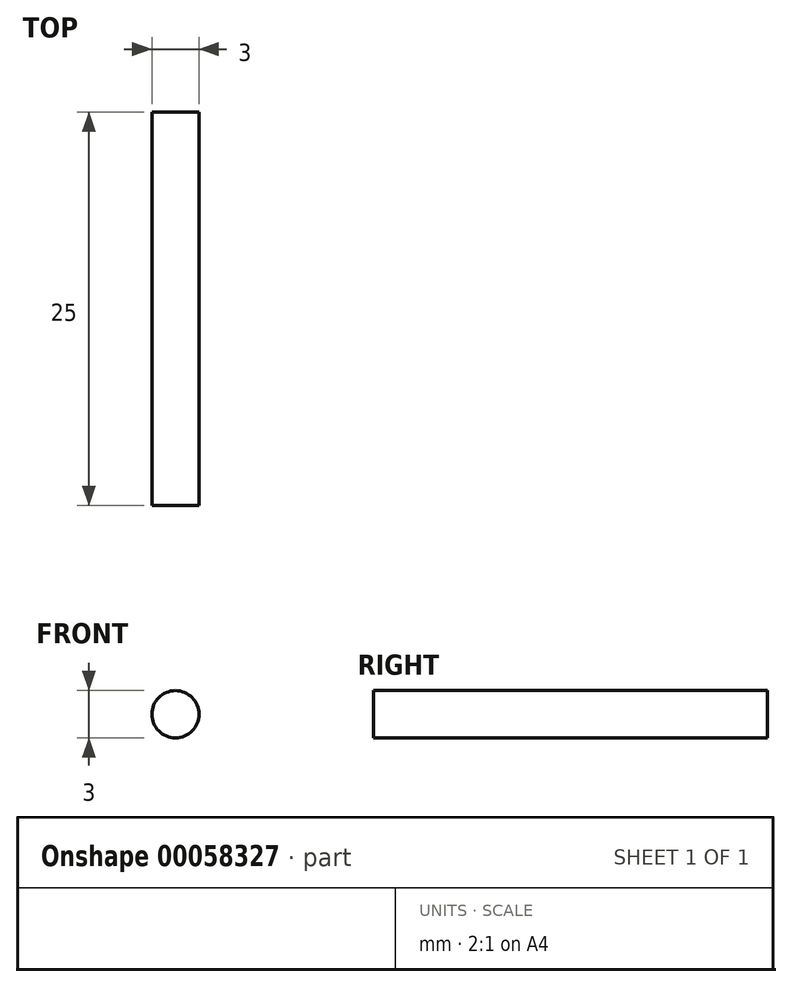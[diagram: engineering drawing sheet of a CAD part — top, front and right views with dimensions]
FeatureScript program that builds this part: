
annotation { "Feature Type Name" : "Feature", "Feature Type Description" : "" }
export const myFeature = defineFeature(function(context is Context, id is Id, definition is map)
    precondition{}
    {
        {
            var Q0;
            Q0=qCreatedBy(makeId("Front.planeOp"),FACE);
            var sketch = newSketch(context, id + "F0", { "sketchPlane" : qUnion([Q0])});
            skCircle(sketch, "E0", {"center": v(-49.36, 39.83) * mm, "radius": 1.5 * mm});
            skSolve(sketch);
        }
        {
            var Q0;
            Q0 = qSketchRegion(id + "F0", true);
            extrude(context, id + "F1", {"entities" : qUnion([Q0]), "depth" : 25 * mm});
        }
    });
